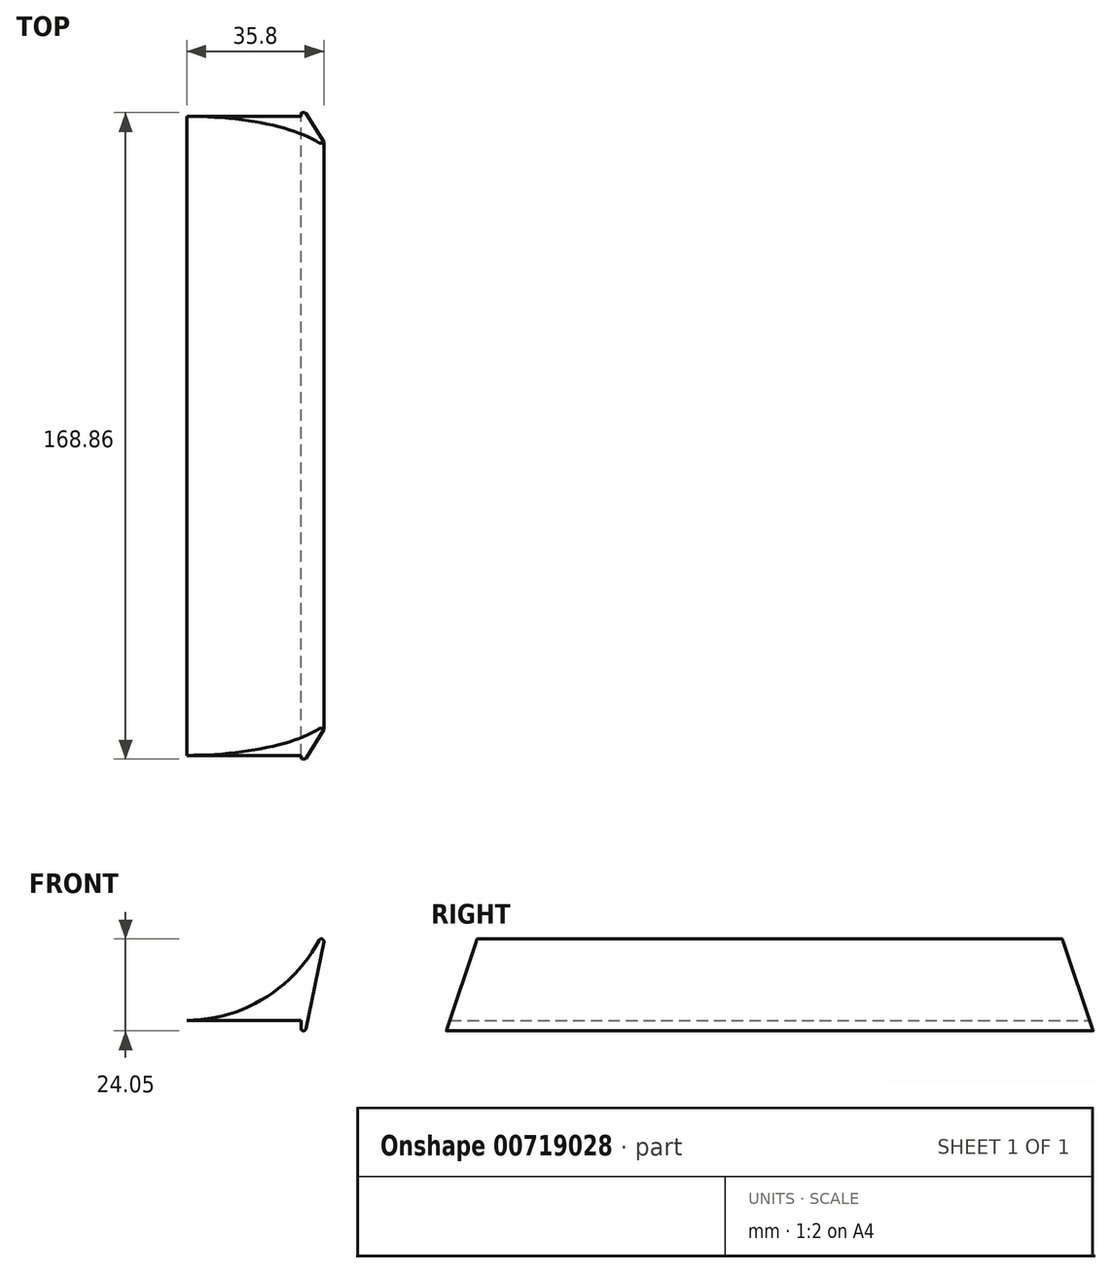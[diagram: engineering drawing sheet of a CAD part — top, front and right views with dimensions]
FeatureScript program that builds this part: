
annotation { "Feature Type Name" : "Feature", "Feature Type Description" : "" }
export const myFeature = defineFeature(function(context is Context, id is Id, definition is map)
    precondition{}
    {
        {
            var Q0;
            Q0=qCreatedBy(makeId("Front.planeOp"),FACE);
            var sketch = newSketch(context, id + "F0", { "sketchPlane" : qUnion([Q0])});
            skArc(sketch, "E0", {"start": v(0, 0) * mm, "mid": v(22.85, 7.47) * mm, "end": v(37.09, 26.83) * mm});
            skLineSegment(sketch, "E1", {"start": v(37.09, 26.83) * mm, "end": v(29.83, -8.52) * mm});
            skLineSegment(sketch, "E2", {"start": v(29.83, -8.52) * mm, "end": v(29.83, 0) * mm});
            skLineSegment(sketch, "E3", {"start": v(29.83, 0) * mm, "end": v(0, 0) * mm});
            skSolve(sketch);
        }
        {
            var Q0;
            Q0 = qSketchRegion(id + "F0", true);
            extrude(context, id + "F1", {"entities" : qUnion([Q0]), "endBound" : BoundingType.SYMMETRIC, "depth" : 173.74 * mm, "offsetDistance" : 25.4 * mm});
        }
        {
            var Q0;
            Q0=makeQuery(id+"F1.opExtrude","SWEPT_EDGE",EDGE,{"disambiguationData":[OSD([sQuery(id+"F0.wireOp",EDGE,"E0"),sQuery(id+"F0.wireOp",EDGE,"E1")])]});
            var Q1;
            Q1=makeQuery(id+"F1.opExtrude","SWEPT_EDGE",EDGE,{"disambiguationData":[OSD([sQuery(id+"F0.wireOp",EDGE,"E1"),sQuery(id+"F0.wireOp",EDGE,"E2")])]});
            fillet(context, id + "F2", {"entities" : qUnion([Q0, Q1]), "radius" : 0.65 * mm, "tangentPropagation" : true, "allowEdgeOverflow" : false});
        }
        {
            var Q0;
            Q0=qCreatedBy(makeId("Right.planeOp"),FACE);
            var sketch = newSketch(context, id + "F3", { "sketchPlane" : qUnion([Q0])});
            skLineSegment(sketch, "E4", {"start": v(-65.26, 54.75) * mm, "end": v(-90.38, -20.59) * mm});
            skLineSegment(sketch, "E5", {"start": v(-90.38, -20.59) * mm, "end": v(-99.72, 31.1) * mm});
            skLineSegment(sketch, "E6", {"start": v(-99.72, 31.1) * mm, "end": v(-65.26, 54.75) * mm});
            skLineSegment(sketch, "E7", {"start": v(0, 60.6) * mm, "end": v(0, -37.81) * mm});
            skLineSegment(sketch, "E8.MirrorCS", {"start": v(65.26, 54.75) * mm, "end": v(90.38, -20.59) * mm});
            skLineSegment(sketch, "E9.MirrorCS", {"start": v(90.38, -20.59) * mm, "end": v(99.72, 31.1) * mm});
            skLineSegment(sketch, "E10.MirrorCS", {"start": v(99.72, 31.1) * mm, "end": v(65.26, 54.75) * mm});
            skSolve(sketch);
        }
        {
            var Q0;
            Q0=makeQuery(id+"F3.imprint","IMPRINT",FACE,{"disambiguationData":[TD([[makeQuery(id+"F3.imprint","IMPRINT",EDGE,{"derivedFrom":sQuery(id+"F3.wireOp",EDGE,"E4")}),-1.0]])]});
            var Q1;
            Q1=makeQuery(id+"F3.imprint","IMPRINT",FACE,{"disambiguationData":[TD([[makeQuery(id+"F3.imprint","IMPRINT",EDGE,{"derivedFrom":sQuery(id+"F3.wireOp",EDGE,"E8.MirrorCS")}),1.0]])]});
            extrude(context, id + "F4", {"entities" : qUnion([Q0, Q1]), "operationType" : NewBodyOperationType.REMOVE, "depth" : 63.25 * mm, "offsetDistance" : 25.4 * mm});
        }
    });
